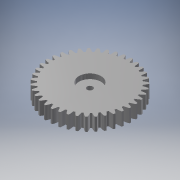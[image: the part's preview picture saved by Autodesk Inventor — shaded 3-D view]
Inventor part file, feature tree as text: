
AUTODESK INVENTOR PART (.ipt)
format: ipt  version: 2017 (Build 210142000, 142)  size: 316,416 bytes
history: native  units: mm (DEFAULTED — no unit token found)
features: sketch x4, extrude x3, plane x3, other x3
ambient origin geometry x8: Origin, YZ Plane, XZ Plane, XY Plane, X Axis, Y Axis, Z Axis, Center Point
bodies: Solid1 (feature_tree)
feature tree (13):
  extrude  "Extrusion1"  Depth=8.0mm TaperAngle=0.0deg
  plane  "Work Plane2"
  plane  "Work Plane8"
  plane  "Work Plane9"
  other  "Spur Gear"
  extrude  "Extrusion2"  Depth=10.0mm TaperAngle=0.0deg
  extrude  "Extrusion3"  Depth=0.805537mm TaperAngle=0.0deg
  sketch  "Sketch1"  dims[d0=51.25mm d1=8.0mm d2=0.0mm]
  sketch  "Sketch2"  dims[d3=48.75mm d4=10.0mm d5=0.0mm]
  other  "Srf1"
  sketch  "Sketch3"  dims[d16=31.875mm d17=0.0mm d34=0.805537mm]
  sketch  "Sketch4"  dims[d39=0.0mm d41=0.0mm d43=31.875mm d46=31.875mm d47=0.0mm d48=0.0mm d49=3.4544mm d50=10.0mm d51=0.0mm d52=13.5mm d53=3.0mm d54=0.0mm]
  other  "Pitch Diameter"
